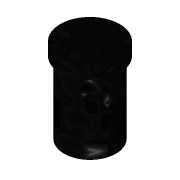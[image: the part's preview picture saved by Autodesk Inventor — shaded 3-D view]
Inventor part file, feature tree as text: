
AUTODESK INVENTOR PART (.ipt)
format: ipt  version: 2022 (Build 260153000, 153)  size: 107,520 bytes
history: native  units: in
note: dims shown in document units (in); Inventor stores cm internally (conversion verified against a paired STEP export)
features: extrude x2, sketch x2
ambient origin geometry x8: Origin, YZ Plane, XZ Plane, XY Plane, X Axis, Y Axis, Z Axis, Center Point
bodies: Solid1 (feature_tree)
feature tree (4):
  extrude  "Extrusion1"  Depth=0.7835in TaperAngle=0.0deg
  extrude  "Extrusion2"  Depth=0.1181in TaperAngle=0.0deg
  sketch  "Sketch1"  dims[d0=0.4803in d1=0.7835in d2=0.0in]
  sketch  "Sketch2"  dims[d3=0.5512in d4=0.1181in d5=0.0in]
